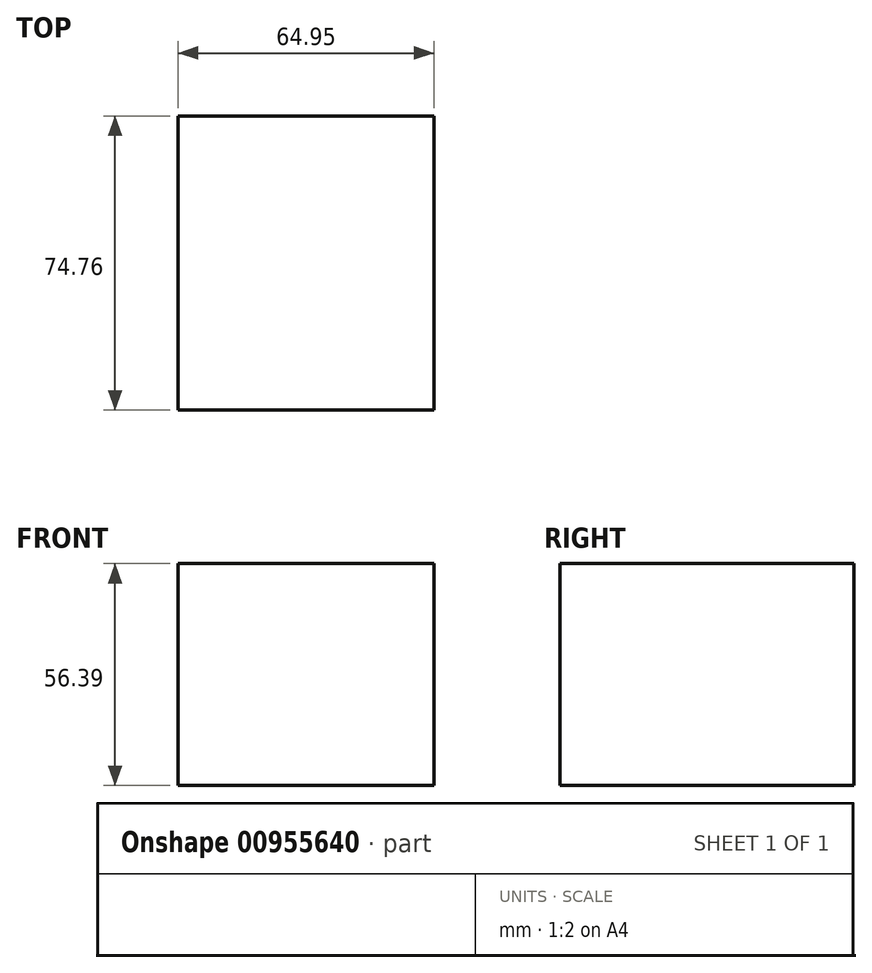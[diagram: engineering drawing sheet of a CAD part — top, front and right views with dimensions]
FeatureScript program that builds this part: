
annotation { "Feature Type Name" : "Feature", "Feature Type Description" : "" }
export const myFeature = defineFeature(function(context is Context, id is Id, definition is map)
    precondition{}
    {
        {
            var Q0;
            Q0=qCreatedBy(makeId("Top.planeOp"),FACE);
            var sketch = newSketch(context, id + "F0", { "sketchPlane" : qUnion([Q0])});
            skLineSegment(sketch, "E0.bottom", {"start": v(0, 0) * mm, "end": v(64.95, 0) * mm});
            skLineSegment(sketch, "E0.top", {"start": v(0, 74.76) * mm, "end": v(64.95, 74.76) * mm});
            skLineSegment(sketch, "E0.left", {"start": v(0, 0) * mm, "end": v(0, 74.76) * mm});
            skLineSegment(sketch, "E0.right", {"start": v(64.95, 0) * mm, "end": v(64.95, 74.76) * mm});
            skSolve(sketch);
        }
        {
            var Q0;
            Q0 = qSketchRegion(id + "F0", true);
            extrude(context, id + "F1", {"entities" : qUnion([Q0]), "depth" : 56.4 * mm, "offsetDistance" : 25.4 * mm});
        }
    });
